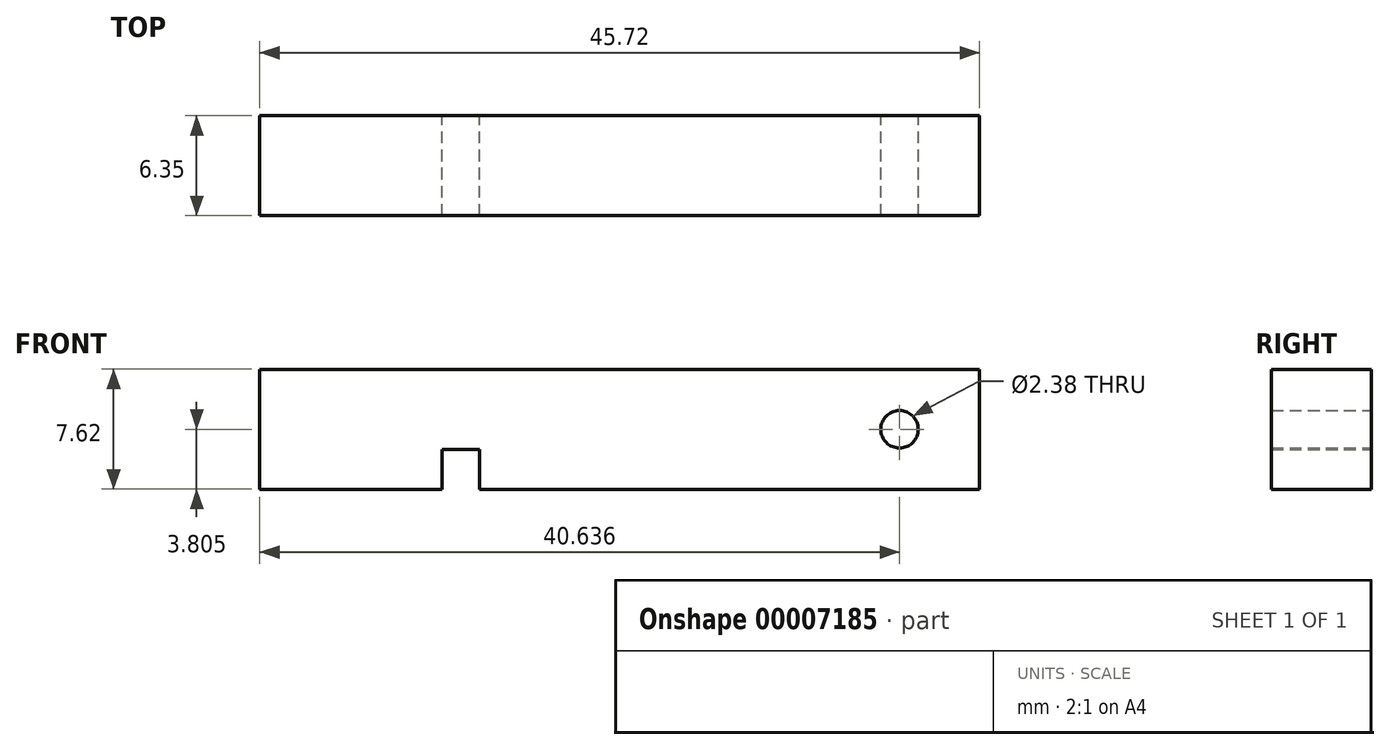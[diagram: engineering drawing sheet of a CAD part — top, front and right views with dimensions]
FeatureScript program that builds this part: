
annotation { "Feature Type Name" : "Feature", "Feature Type Description" : "" }
export const myFeature = defineFeature(function(context is Context, id is Id, definition is map)
    precondition{}
    {
        {
            var Q0;
            Q0=qCreatedBy(makeId("Front.planeOp"),FACE);
            var sketch = newSketch(context, id + "F0", { "sketchPlane" : qUnion([Q0])});
            skLineSegment(sketch, "E0.bottom", {"start": v(-9.7, 3.3) * mm, "end": v(36.02, 3.3) * mm});
            skLineSegment(sketch, "E0.top", {"start": v(-9.7, -4.32) * mm, "end": v(1.87, -4.32) * mm});
            skLineSegment(sketch, "E0.left", {"start": v(-9.7, 3.3) * mm, "end": v(-9.7, -4.32) * mm});
            skLineSegment(sketch, "E0.right", {"start": v(36.02, 3.3) * mm, "end": v(36.02, -4.32) * mm});
            skPoint(sketch, "E1", {"position": v(36.02, -0.51) * mm});
            skCircle(sketch, "E2", {"center": v(30.94, -0.51) * mm, "radius": 1.2 * mm});
            skLineSegment(sketch, "E3.top", {"start": v(1.87, -1.78) * mm, "end": v(4.27, -1.78) * mm});
            skLineSegment(sketch, "E3.left", {"start": v(1.87, -4.32) * mm, "end": v(1.87, -1.78) * mm});
            skLineSegment(sketch, "E3.right", {"start": v(4.27, -4.32) * mm, "end": v(4.27, -1.78) * mm});
            skLineSegment(sketch, "E4.trimOffspring", {"start": v(4.27, -4.32) * mm, "end": v(36.02, -4.32) * mm});
            skSolve(sketch);
        }
        {
            var Q0;
            Q0=makeQuery(id+"F0.imprint","IMPRINT",FACE,{"disambiguationData":[TD([[makeQuery(id+"F0.imprint","IMPRINT",EDGE,{"derivedFrom":sQuery(id+"F0.wireOp",EDGE,"E0.bottom")}),-1.0]])]});
            extrude(context, id + "F1", {"entities" : qUnion([Q0]), "depth" : 6.35 * mm});
        }
    });
